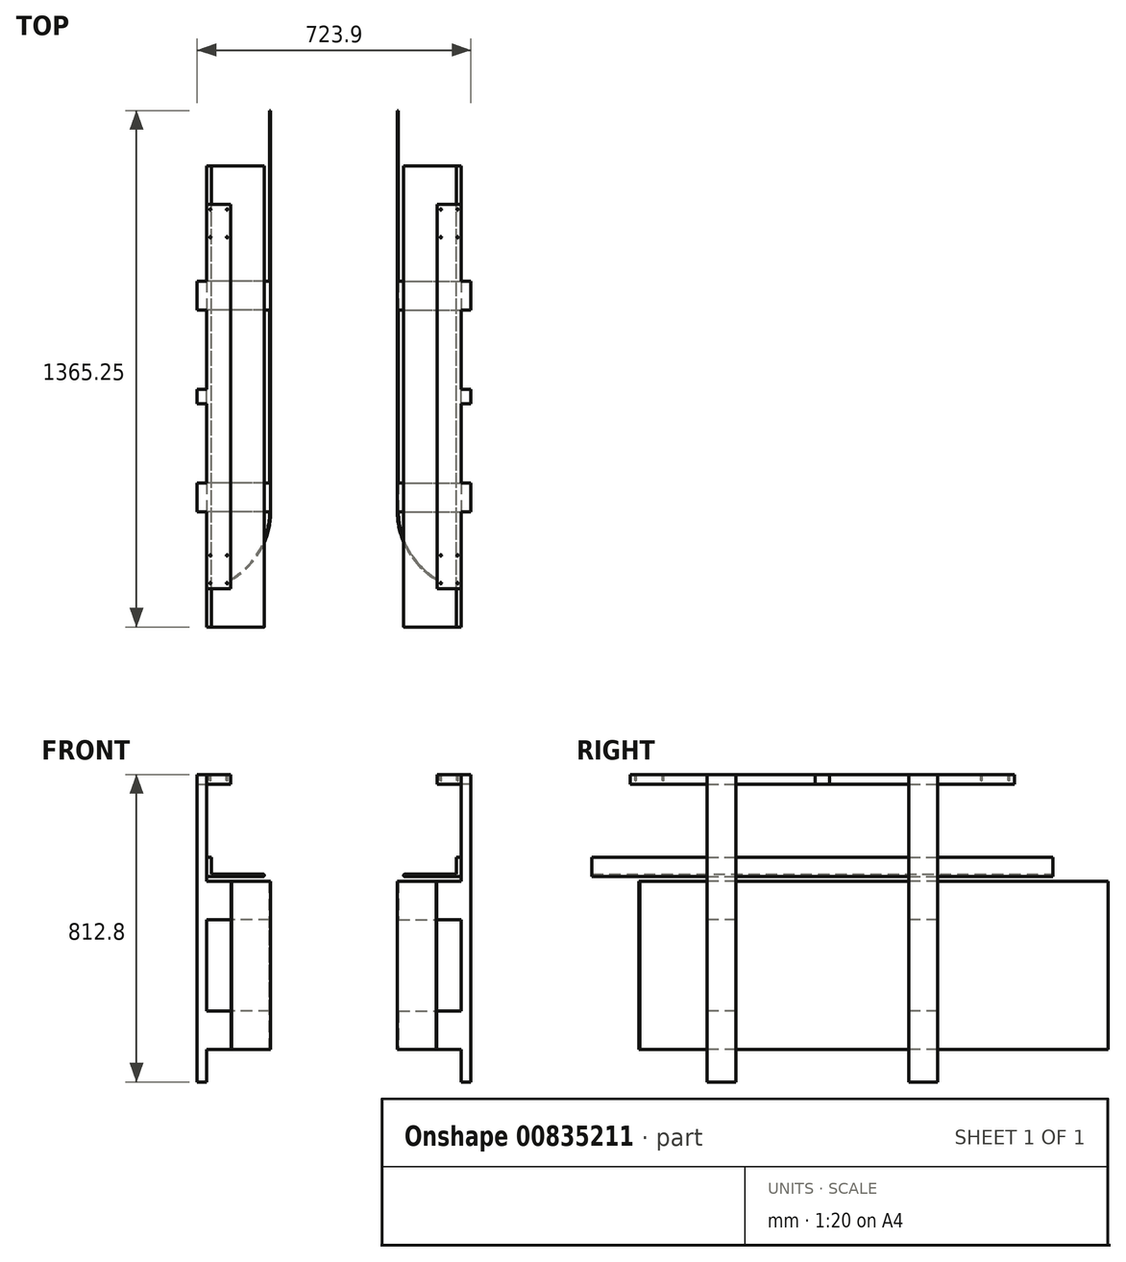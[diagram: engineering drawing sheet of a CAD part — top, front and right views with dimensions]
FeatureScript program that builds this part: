
annotation { "Feature Type Name" : "Feature", "Feature Type Description" : "" }
export const myFeature = defineFeature(function(context is Context, id is Id, definition is map)
    precondition{}
    {
        {
            var Q0;
            Q0=qCreatedBy(makeId("Front.planeOp"),FACE);
            var sketch = newSketch(context, id + "F0", { "sketchPlane" : qUnion([Q0])});
            skLineSegment(sketch, "E0.bottom", {"start": v(31.75, 12.7) * mm, "end": v(-31.75, 12.7) * mm});
            skLineSegment(sketch, "E0.top", {"start": v(31.75, -12.7) * mm, "end": v(-31.75, -12.7) * mm});
            skLineSegment(sketch, "E0.left", {"start": v(31.75, 12.7) * mm, "end": v(31.75, -12.7) * mm});
            skLineSegment(sketch, "E0.right", {"start": v(-31.75, 12.7) * mm, "end": v(-31.75, -12.7) * mm});
            skPoint(sketch, "E0.middle", {"position": v(0, 0) * mm});
            skSolve(sketch);
        }
        {
            var Q0;
            Q0 = qSketchRegion(id + "F0", true);
            extrude(context, id + "F1", {"entities" : qUnion([Q0]), "endBound" : BoundingType.SYMMETRIC, "depth" : 1016 * mm, "offsetDistance" : 25.4 * mm});
        }
        {
            var Q0;
            Q0=makeQuery(id+"F1.opExtrude","SWEPT_FACE",FACE,{"disambiguationData":[OSD([sQuery(id+"F0.wireOp",EDGE,"E0.left")])]});
            var sketch = newSketch(context, id + "F2", { "sketchPlane" : qUnion([Q0])});
            skLineSegment(sketch, "E1.bottom", {"start": v(-304.8, 12.7) * mm, "end": v(-228.6, 12.7) * mm});
            skLineSegment(sketch, "E1.top", {"start": v(-304.8, -800.1) * mm, "end": v(-228.6, -800.1) * mm});
            skLineSegment(sketch, "E1.left", {"start": v(-304.8, 12.7) * mm, "end": v(-304.8, -800.1) * mm});
            skLineSegment(sketch, "E1.right", {"start": v(-228.6, 12.7) * mm, "end": v(-228.6, -800.1) * mm});
            skLineSegment(sketch, "E2.bottom", {"start": v(228.6, 12.7) * mm, "end": v(304.8, 12.7) * mm});
            skLineSegment(sketch, "E2.top", {"start": v(228.6, -800.1) * mm, "end": v(304.8, -800.1) * mm});
            skLineSegment(sketch, "E2.left", {"start": v(228.6, 12.7) * mm, "end": v(228.6, -800.1) * mm});
            skLineSegment(sketch, "E2.right", {"start": v(304.8, 12.7) * mm, "end": v(304.8, -800.1) * mm});
            skSolve(sketch);
        }
        {
            var Q0;
            Q0 = qSketchRegion(id + "F2", true);
            extrude(context, id + "F3", {"entities" : qUnion([Q0]), "operationType" : NewBodyOperationType.ADD, "depth" : 25.4 * mm, "offsetDistance" : 25.4 * mm});
        }
        {
            var Q0;
            Q0=makeQuery(id+"F3.boolean.opBoolean","MERGE",FACE,{"derivedFrom":[makeQuery(id+"F1.opExtrude","SWEPT_FACE",FACE,{"disambiguationData":[OSD([sQuery(id+"F0.wireOp",EDGE,"E0.bottom")])]}),makeQuery(id+"F3.opExtrude","SWEPT_FACE",FACE,{"disambiguationData":[OSD([sQuery(id+"F2.wireOp",EDGE,"E1.bottom")])]}),makeQuery(id+"F3.opExtrude","SWEPT_FACE",FACE,{"disambiguationData":[OSD([sQuery(id+"F2.wireOp",EDGE,"E2.bottom")])]})]});
            var sketch = newSketch(context, id + "F4", { "sketchPlane" : qUnion([Q0])});
            skPoint(sketch, "E3", {"position": v(22.22, 493.71) * mm});
            skPoint(sketch, "E4", {"position": v(-22.23, 493.71) * mm});
            skPoint(sketch, "E5", {"position": v(22.22, -493.71) * mm});
            skPoint(sketch, "E6", {"position": v(-22.22, -493.71) * mm});
            skPoint(sketch, "E7", {"position": v(-22.23, 420.69) * mm});
            skPoint(sketch, "E8", {"position": v(22.22, 420.69) * mm});
            skPoint(sketch, "E9", {"position": v(22.22, -420.69) * mm});
            skPoint(sketch, "E10", {"position": v(-22.22, -420.69) * mm});
            skSolve(sketch);
        }
        {
            var Q0;
            Q0=sQuery(id+"F4.wireOp",VERTEX,"E8");
            var Q1;
            Q1=sQuery(id+"F4.wireOp",VERTEX,"E7");
            var Q2;
            Q2=sQuery(id+"F4.wireOp",VERTEX,"E3");
            var Q3;
            Q3=sQuery(id+"F4.wireOp",VERTEX,"E4");
            var Q4;
            Q4=sQuery(id+"F4.wireOp",VERTEX,"E9");
            var Q5;
            Q5=sQuery(id+"F4.wireOp",VERTEX,"E10");
            var Q6;
            Q6=sQuery(id+"F4.wireOp",VERTEX,"E6");
            var Q7;
            Q7=sQuery(id+"F4.wireOp",VERTEX,"E5");
            var Q8;
            Q8=makeQuery(id+"F1.opExtrude","SWEPT_BODY",BODY,{"disambiguationData":[OSD([sQuery(id+"F0.wireOp",EDGE,"E0.bottom"),sQuery(id+"F0.wireOp",EDGE,"E0.top"),sQuery(id+"F0.wireOp",EDGE,"E0.left"),sQuery(id+"F0.wireOp",EDGE,"E0.right")])]});
            hole(context, id + "F5", {"style" : HoleStyle.SIMPLE, "endStyle" : HoleEndStyle.BLIND, "standardTappedOrClearance" : lookupTablePath({ "standard" : "ANSI", "engagement" : "75%", "pitch" : "24 tpi", "size" : "#10", "type" : "Tapped" }), "standardBlindInLast" : lookupTablePath({ "standard" : "ANSI", "engagement" : "75%", "pitch" : "24 tpi", "size" : "#10", "type" : "Tapped" }), "holeDiameter" : 3.8 * mm, "majorDiameter" : 4.83 * mm, "showTappedDepth" : true, "holeDepth" : 15.88 * mm, "isTappedThrough" : true, "tappedDepth" : 12.7 * mm, "tapClearance" : 3, "startFromSketch" : true, "locations" : qUnion([Q0, Q1, Q2, Q3, Q4, Q5, Q6, Q7]), "scope" : qUnion([Q8])});
        }
        {
            var Q0;
            Q0=qCreatedBy(makeId("Front.planeOp"),FACE);
            var sketch = newSketch(context, id + "F6", { "sketchPlane" : qUnion([Q0])});
            skLineSegment(sketch, "E11", {"start": v(31.75, -257.18) * mm, "end": v(-120.65, -257.18) * mm});
            skLineSegment(sketch, "E12", {"start": v(-120.65, -257.18) * mm, "end": v(-120.65, -250.82) * mm});
            skLineSegment(sketch, "E13", {"start": v(-120.65, -250.83) * mm, "end": v(19.05, -250.83) * mm});
            skLineSegment(sketch, "E14", {"start": v(19.05, -250.83) * mm, "end": v(19.05, -206.38) * mm});
            skLineSegment(sketch, "E15", {"start": v(19.05, -206.38) * mm, "end": v(31.75, -206.38) * mm});
            skLineSegment(sketch, "E16", {"start": v(31.75, -206.38) * mm, "end": v(31.75, -257.18) * mm});
            skSolve(sketch);
        }
        {
            var Q0;
            Q0 = qSketchRegion(id + "F6", true);
            extrude(context, id + "F7", {"entities" : qUnion([Q0]), "operationType" : NewBodyOperationType.ADD, "endBound" : BoundingType.SYMMETRIC, "depth" : 1219.2 * mm, "offsetDistance" : 25.4 * mm});
        }
        {
            var Q0;
            Q0=makeQuery(id+"F7.opExtrude","SWEPT_EDGE",EDGE,{"disambiguationData":[OSD([sQuery(id+"F6.wireOp",EDGE,"E11"),sQuery(id+"F6.wireOp",EDGE,"E12")])]});
            var Q1;
            Q1=makeQuery(id+"F7.opExtrude","SWEPT_EDGE",EDGE,{"disambiguationData":[OSD([sQuery(id+"F6.wireOp",EDGE,"E12"),sQuery(id+"F6.wireOp",EDGE,"E13")])]});
            fillet(context, id + "F8", {"entities" : qUnion([Q0, Q1]), "radius" : 3.17 * mm, "tangentPropagation" : true, "allowEdgeOverflow" : false});
        }
        {
            var Q0;
            {var subQ0=sQuery(id+"F2.wireOp",EDGE,"E2.right");var subQ1=sQuery(id+"F2.wireOp",EDGE,"E2.left");var subQ2=sQuery(id+"F2.wireOp",EDGE,"E2.top");Q0=makeQuery(id+"F7.boolean.opBoolean","SPLIT",FACE,{"disambiguationData":[TD([makeQuery(id+"F3.opExtrude","SWEPT_FACE",FACE,{"disambiguationData":[OSD([subQ2])]})])],"derivedFrom":makeQuery(id+"F3.opExtrude","CAP_FACE",FACE,{"disambiguationData":[OSD([sQuery(id+"F2.wireOp",EDGE,"E2.bottom"),subQ2,subQ1,subQ0])],"isStart":true})});}
            var sketch = newSketch(context, id + "F9", { "sketchPlane" : qUnion([Q0])});
            skLineSegment(sketch, "E17.bottom", {"start": v(-304.8, -269.88) * mm, "end": v(-228.6, -269.88) * mm});
            skLineSegment(sketch, "E17.top", {"start": v(-304.8, -371.48) * mm, "end": v(-228.6, -371.48) * mm});
            skLineSegment(sketch, "E17.left", {"start": v(-304.8, -269.88) * mm, "end": v(-304.8, -371.48) * mm});
            skLineSegment(sketch, "E17.right", {"start": v(-228.6, -269.88) * mm, "end": v(-228.6, -371.48) * mm});
            skLineSegment(sketch, "E18.bottom", {"start": v(228.6, -269.88) * mm, "end": v(304.8, -269.88) * mm});
            skLineSegment(sketch, "E18.top", {"start": v(228.6, -371.48) * mm, "end": v(304.8, -371.48) * mm});
            skLineSegment(sketch, "E18.left", {"start": v(228.6, -269.88) * mm, "end": v(228.6, -371.48) * mm});
            skLineSegment(sketch, "E18.right", {"start": v(304.8, -269.88) * mm, "end": v(304.8, -371.48) * mm});
            skLineSegment(sketch, "E19.bottom", {"start": v(-304.8, -612.78) * mm, "end": v(-228.6, -612.78) * mm});
            skLineSegment(sketch, "E19.top", {"start": v(-304.8, -714.38) * mm, "end": v(-228.6, -714.38) * mm});
            skLineSegment(sketch, "E19.left", {"start": v(-304.8, -612.78) * mm, "end": v(-304.8, -714.38) * mm});
            skLineSegment(sketch, "E19.right", {"start": v(-228.6, -612.78) * mm, "end": v(-228.6, -714.38) * mm});
            skLineSegment(sketch, "E20.bottom", {"start": v(228.6, -612.78) * mm, "end": v(304.8, -612.78) * mm});
            skLineSegment(sketch, "E20.top", {"start": v(228.6, -714.38) * mm, "end": v(304.8, -714.38) * mm});
            skLineSegment(sketch, "E20.left", {"start": v(228.6, -612.78) * mm, "end": v(228.6, -714.38) * mm});
            skLineSegment(sketch, "E20.right", {"start": v(304.8, -612.78) * mm, "end": v(304.8, -714.38) * mm});
            skSolve(sketch);
        }
        {
            var Q0;
            Q0 = qSketchRegion(id + "F9", true);
            extrude(context, id + "F10", {"entities" : qUnion([Q0]), "operationType" : NewBodyOperationType.ADD, "depth" : 166.37 * mm, "offsetDistance" : 25.4 * mm});
        }
        {
            var Q0;
            Q0=makeQuery(id+"F10.opExtrude","SWEPT_FACE",FACE,{"disambiguationData":[OSD([sQuery(id+"F9.wireOp",EDGE,"E17.bottom")])]});
            var sketch = newSketch(context, id + "F11", { "sketchPlane" : qUnion([Q0])});
            skLineSegment(sketch, "E21", {"start": v(-134.62, -304.8) * mm, "end": v(-134.62, 755.65) * mm});
            skLineSegment(sketch, "E22", {"start": v(-137.29, -304.8) * mm, "end": v(-137.29, 755.65) * mm});
            skLineSegment(sketch, "E23", {"start": v(-137.29, 755.65) * mm, "end": v(-134.62, 755.65) * mm});
            skArc(sketch, "E24", {"start": v(-134.62, -304.8) * mm, "mid": v(-107.43, -407.2) * mm, "end": v(-33.02, -482.6) * mm});
            skArc(sketch, "E25", {"start": v(-137.29, -304.8) * mm, "mid": v(-109.74, -408.51) * mm, "end": v(-34.37, -484.9) * mm});
            skLineSegment(sketch, "E26", {"start": v(-33.02, -482.6) * mm, "end": v(81.58, -550.13) * mm, "construction": true});
            skLineSegment(sketch, "E27", {"start": v(-33.02, -482.6) * mm, "end": v(-34.37, -484.9) * mm});
            skSolve(sketch);
        }
        {
            var Q0;
            Q0 = qSketchRegion(id + "F11", true);
            var Q1;
            Q1=makeQuery(id+"F10.opExtrude","SWEPT_FACE",FACE,{"disambiguationData":[OSD([sQuery(id+"F9.wireOp",EDGE,"E20.top")])]});
            extrude(context, id + "F12", {"entities" : qUnion([Q0]), "operationType" : NewBodyOperationType.ADD, "endBound" : BoundingType.UP_TO_SURFACE, "oppositeDirection" : true, "depth" : 25.4 * mm, "endBoundEntityFace" : qUnion([Q1]), "offsetDistance" : 25.4 * mm});
        }
        {
            var Q0;
            {var subQ0=sQuery(id+"F2.wireOp",EDGE,"E1.right");Q0=makeQuery(id+"F3.boolean.opBoolean","SPLIT",FACE,{"disambiguationData":[TD([makeQuery(id+"F3.opExtrude","SWEPT_FACE",FACE,{"disambiguationData":[OSD([subQ0])]})])],"derivedFrom":makeQuery(id+"F1.opExtrude","SWEPT_FACE",FACE,{"disambiguationData":[OSD([sQuery(id+"F0.wireOp",EDGE,"E0.left")])]})});}
            var sketch = newSketch(context, id + "F13", { "sketchPlane" : qUnion([Q0])});
            skLineSegment(sketch, "E28.bottom", {"start": v(19.05, 12.7) * mm, "end": v(-19.05, 12.7) * mm});
            skLineSegment(sketch, "E28.top", {"start": v(19.05, -12.7) * mm, "end": v(-19.05, -12.7) * mm});
            skLineSegment(sketch, "E28.left", {"start": v(19.05, 12.7) * mm, "end": v(19.05, -12.7) * mm});
            skLineSegment(sketch, "E28.right", {"start": v(-19.05, 12.7) * mm, "end": v(-19.05, -12.7) * mm});
            skPoint(sketch, "E28.middle", {"position": v(0, 0) * mm});
            skSolve(sketch);
        }
        {
            var Q0;
            Q0 = qSketchRegion(id + "F13", true);
            var Q1;
            Q1=makeQuery(id+"F3.opExtrude","CAP_FACE",FACE,{"disambiguationData":[OSD([sQuery(id+"F2.wireOp",EDGE,"E2.bottom"),sQuery(id+"F2.wireOp",EDGE,"E2.top"),sQuery(id+"F2.wireOp",EDGE,"E2.left"),sQuery(id+"F2.wireOp",EDGE,"E2.right")])],"isStart":false});
            extrude(context, id + "F14", {"entities" : qUnion([Q0]), "operationType" : NewBodyOperationType.ADD, "endBound" : BoundingType.UP_TO_SURFACE, "depth" : 25.4 * mm, "endBoundEntityFace" : qUnion([Q1]), "offsetDistance" : 25.4 * mm});
        }
        {
            var Q0;
            Q0=qCreatedBy(makeId("Right.planeOp"),FACE);
            cPlane(context, id + "F15", {"entities" : qUnion([Q0]), "cplaneType" : CPlaneType.OFFSET, "offset" : 304.8 * mm, "oppositeDirection" : true, "width" : 152.4 * mm, "height" : 152.4 * mm});
        }
        {
            var Q0;
            Q0=makeQuery(id+"F1.opExtrude","SWEPT_BODY",BODY,{"disambiguationData":[OSD([sQuery(id+"F0.wireOp",EDGE,"E0.bottom"),sQuery(id+"F0.wireOp",EDGE,"E0.top"),sQuery(id+"F0.wireOp",EDGE,"E0.left"),sQuery(id+"F0.wireOp",EDGE,"E0.right")])]});
            var Q1;
            Q1=qCreatedBy(id+"F15.planeOp",FACE);
            mirror(context, id + "F16", {"entities" : qUnion([Q0]), "mirrorPlane" : qUnion([Q1])});
        }
    });
